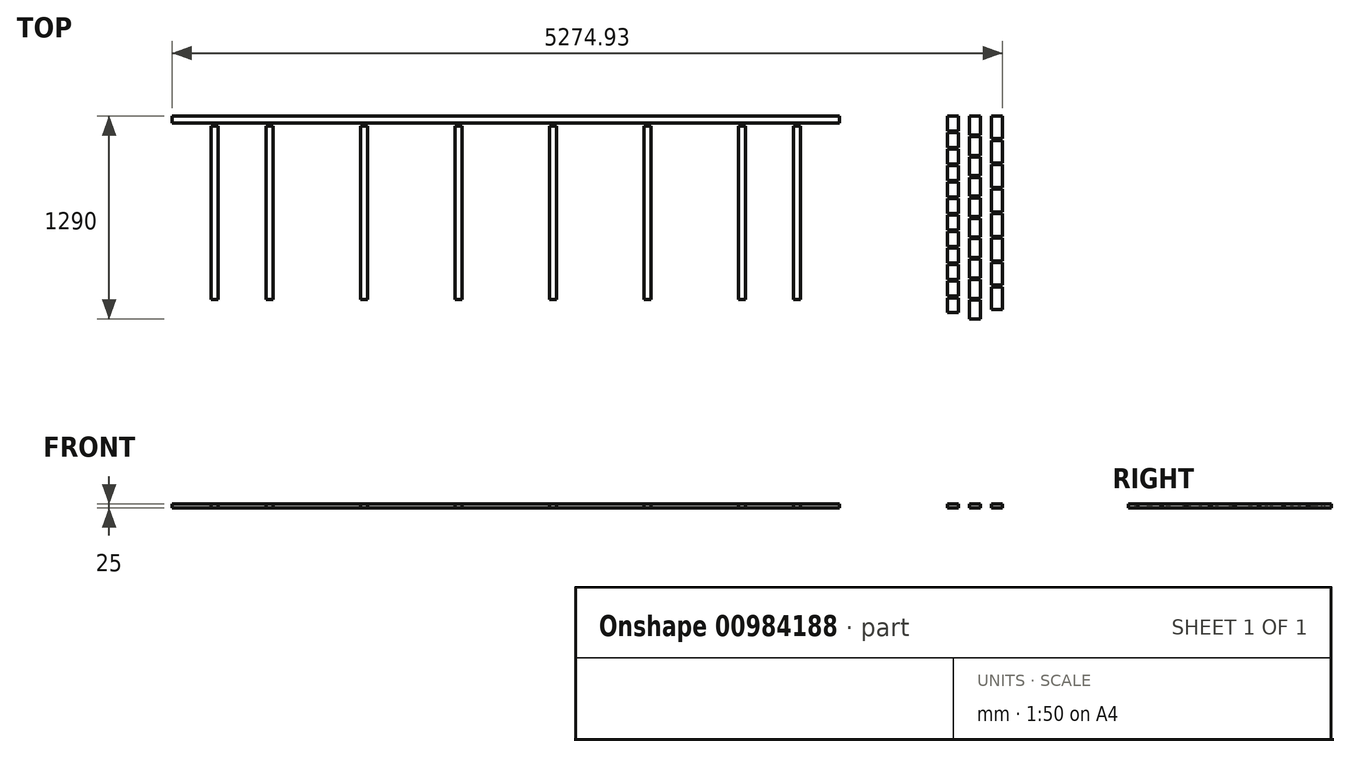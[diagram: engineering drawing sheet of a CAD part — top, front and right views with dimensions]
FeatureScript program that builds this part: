
annotation { "Feature Type Name" : "Feature", "Feature Type Description" : "" }
export const myFeature = defineFeature(function(context is Context, id is Id, definition is map)
    precondition{}
    {
        {
            var Q0;
            Q0=qCreatedBy(makeId("Top.planeOp"),FACE);
            var sketch = newSketch(context, id + "F0", { "sketchPlane" : qUnion([Q0])});
            skLineSegment(sketch, "E0.bottom", {"start": v(-2120, 45) * mm, "end": v(2120, 45) * mm});
            skLineSegment(sketch, "E0.top", {"start": v(-2120, 0) * mm, "end": v(2120, 0) * mm});
            skLineSegment(sketch, "E0.left", {"start": v(-2120, 45) * mm, "end": v(-2120, 0) * mm});
            skLineSegment(sketch, "E0.right", {"start": v(2120, 45) * mm, "end": v(2120, 0) * mm});
            skLineSegment(sketch, "E1.top", {"start": v(-1522.5, -1120) * mm, "end": v(-1477.5, -1120) * mm});
            skLineSegment(sketch, "E1.left", {"start": v(-1522.5, -20) * mm, "end": v(-1522.5, -1120) * mm});
            skLineSegment(sketch, "E1.right", {"start": v(-1477.5, -20) * mm, "end": v(-1477.5, -1120) * mm});
            skLineSegment(sketch, "E2.bottom", {"start": v(2804.93, 45) * mm, "end": v(2874.93, 45) * mm});
            skLineSegment(sketch, "E2.top", {"start": v(2804.93, -50) * mm, "end": v(2874.93, -50) * mm});
            skLineSegment(sketch, "E2.left", {"start": v(2804.93, 45) * mm, "end": v(2804.93, -50) * mm});
            skLineSegment(sketch, "E2.right", {"start": v(2874.93, 45) * mm, "end": v(2874.93, -50) * mm});
            skLineSegment(sketch, "E3.0.1.0", {"start": v(2804.93, -60) * mm, "end": v(2804.93, -155) * mm});
            skLineSegment(sketch, "E3.0.1.1", {"start": v(2804.93, -60) * mm, "end": v(2874.93, -60) * mm});
            skLineSegment(sketch, "E3.0.1.2", {"start": v(2804.93, -155) * mm, "end": v(2874.93, -155) * mm});
            skLineSegment(sketch, "E3.0.1.3", {"start": v(2874.93, -60) * mm, "end": v(2874.93, -155) * mm});
            skLineSegment(sketch, "E3.0.2.0", {"start": v(2804.93, -165) * mm, "end": v(2804.93, -260) * mm});
            skLineSegment(sketch, "E3.0.2.1", {"start": v(2804.93, -165) * mm, "end": v(2874.93, -165) * mm});
            skLineSegment(sketch, "E3.0.2.2", {"start": v(2804.93, -260) * mm, "end": v(2874.93, -260) * mm});
            skLineSegment(sketch, "E3.0.2.3", {"start": v(2874.93, -165) * mm, "end": v(2874.93, -260) * mm});
            skLineSegment(sketch, "E3.0.3.0", {"start": v(2804.93, -270) * mm, "end": v(2804.93, -365) * mm});
            skLineSegment(sketch, "E3.0.3.1", {"start": v(2804.93, -270) * mm, "end": v(2874.93, -270) * mm});
            skLineSegment(sketch, "E3.0.3.2", {"start": v(2804.93, -365) * mm, "end": v(2874.93, -365) * mm});
            skLineSegment(sketch, "E3.0.3.3", {"start": v(2874.93, -270) * mm, "end": v(2874.93, -365) * mm});
            skLineSegment(sketch, "E3.0.4.0", {"start": v(2804.93, -375) * mm, "end": v(2804.93, -470) * mm});
            skLineSegment(sketch, "E3.0.4.1", {"start": v(2804.93, -375) * mm, "end": v(2874.93, -375) * mm});
            skLineSegment(sketch, "E3.0.4.2", {"start": v(2804.93, -470) * mm, "end": v(2874.93, -470) * mm});
            skLineSegment(sketch, "E3.0.4.3", {"start": v(2874.93, -375) * mm, "end": v(2874.93, -470) * mm});
            skLineSegment(sketch, "E3.0.5.0", {"start": v(2804.93, -480) * mm, "end": v(2804.93, -575) * mm});
            skLineSegment(sketch, "E3.0.5.1", {"start": v(2804.93, -480) * mm, "end": v(2874.93, -480) * mm});
            skLineSegment(sketch, "E3.0.5.2", {"start": v(2804.93, -575) * mm, "end": v(2874.93, -575) * mm});
            skLineSegment(sketch, "E3.0.5.3", {"start": v(2874.93, -480) * mm, "end": v(2874.93, -575) * mm});
            skLineSegment(sketch, "E3.0.6.0", {"start": v(2804.93, -585) * mm, "end": v(2804.93, -680) * mm});
            skLineSegment(sketch, "E3.0.6.1", {"start": v(2804.93, -585) * mm, "end": v(2874.93, -585) * mm});
            skLineSegment(sketch, "E3.0.6.2", {"start": v(2804.93, -680) * mm, "end": v(2874.93, -680) * mm});
            skLineSegment(sketch, "E3.0.6.3", {"start": v(2874.93, -585) * mm, "end": v(2874.93, -680) * mm});
            skLineSegment(sketch, "E3.0.7.0", {"start": v(2804.93, -690) * mm, "end": v(2804.93, -785) * mm});
            skLineSegment(sketch, "E3.0.7.1", {"start": v(2804.93, -690) * mm, "end": v(2874.93, -690) * mm});
            skLineSegment(sketch, "E3.0.7.2", {"start": v(2804.93, -785) * mm, "end": v(2874.93, -785) * mm});
            skLineSegment(sketch, "E3.0.7.3", {"start": v(2874.93, -690) * mm, "end": v(2874.93, -785) * mm});
            skLineSegment(sketch, "E3.0.8.0", {"start": v(2804.93, -795) * mm, "end": v(2804.93, -890) * mm});
            skLineSegment(sketch, "E3.0.8.1", {"start": v(2804.93, -795) * mm, "end": v(2874.93, -795) * mm});
            skLineSegment(sketch, "E3.0.8.2", {"start": v(2804.93, -890) * mm, "end": v(2874.93, -890) * mm});
            skLineSegment(sketch, "E3.0.8.3", {"start": v(2874.93, -795) * mm, "end": v(2874.93, -890) * mm});
            skLineSegment(sketch, "E3.0.9.0", {"start": v(2804.93, -900) * mm, "end": v(2804.93, -995) * mm});
            skLineSegment(sketch, "E3.0.9.1", {"start": v(2804.93, -900) * mm, "end": v(2874.93, -900) * mm});
            skLineSegment(sketch, "E3.0.9.2", {"start": v(2804.93, -995) * mm, "end": v(2874.93, -995) * mm});
            skLineSegment(sketch, "E3.0.9.3", {"start": v(2874.93, -900) * mm, "end": v(2874.93, -995) * mm});
            skLineSegment(sketch, "E3.0.10.0", {"start": v(2804.93, -1005) * mm, "end": v(2804.93, -1100) * mm});
            skLineSegment(sketch, "E3.0.10.1", {"start": v(2804.93, -1005) * mm, "end": v(2874.93, -1005) * mm});
            skLineSegment(sketch, "E3.0.10.2", {"start": v(2804.93, -1100) * mm, "end": v(2874.93, -1100) * mm});
            skLineSegment(sketch, "E3.0.10.3", {"start": v(2874.93, -1005) * mm, "end": v(2874.93, -1100) * mm});
            skLineSegment(sketch, "E3.0.11.0", {"start": v(2804.93, -1110) * mm, "end": v(2804.93, -1205) * mm});
            skLineSegment(sketch, "E3.0.11.1", {"start": v(2804.93, -1110) * mm, "end": v(2874.93, -1110) * mm});
            skLineSegment(sketch, "E3.0.11.2", {"start": v(2804.93, -1205) * mm, "end": v(2874.93, -1205) * mm});
            skLineSegment(sketch, "E3.0.11.3", {"start": v(2874.93, -1110) * mm, "end": v(2874.93, -1205) * mm});
            skLineSegment(sketch, "E3.direction1", {"start": v(2531.99, -50) * mm, "end": v(2804.93, -50) * mm, "construction": true});
            skLineSegment(sketch, "E3.direction2", {"start": v(2804.93, -50) * mm, "end": v(2804.93, -155) * mm, "construction": true});
            skLineSegment(sketch, "E4.1.0.0", {"start": v(-922.5, -20) * mm, "end": v(-922.5, -1120) * mm});
            skLineSegment(sketch, "E4.1.0.1", {"start": v(-877.5, -20) * mm, "end": v(-877.5, -1120) * mm});
            skLineSegment(sketch, "E4.1.0.2", {"start": v(-922.5, -1120) * mm, "end": v(-877.5, -1120) * mm});
            skLineSegment(sketch, "E4.1.0.3", {"start": v(-922.5, -20) * mm, "end": v(-877.5, -20) * mm});
            skLineSegment(sketch, "E4.2.0.0", {"start": v(-322.5, -20) * mm, "end": v(-322.5, -1120) * mm});
            skLineSegment(sketch, "E4.2.0.1", {"start": v(-277.5, -20) * mm, "end": v(-277.5, -1120) * mm});
            skLineSegment(sketch, "E4.2.0.2", {"start": v(-322.5, -1120) * mm, "end": v(-277.5, -1120) * mm});
            skLineSegment(sketch, "E4.2.0.3", {"start": v(-322.5, -20) * mm, "end": v(-277.5, -20) * mm});
            skLineSegment(sketch, "E4.3.0.0", {"start": v(277.5, -20) * mm, "end": v(277.5, -1120) * mm});
            skLineSegment(sketch, "E4.3.0.1", {"start": v(322.5, -20) * mm, "end": v(322.5, -1120) * mm});
            skLineSegment(sketch, "E4.3.0.2", {"start": v(277.5, -1120) * mm, "end": v(322.5, -1120) * mm});
            skLineSegment(sketch, "E4.3.0.3", {"start": v(277.5, -20) * mm, "end": v(322.5, -20) * mm});
            skLineSegment(sketch, "E4.4.0.0", {"start": v(877.5, -20) * mm, "end": v(877.5, -1120) * mm});
            skLineSegment(sketch, "E4.4.0.1", {"start": v(922.5, -20) * mm, "end": v(922.5, -1120) * mm});
            skLineSegment(sketch, "E4.4.0.2", {"start": v(877.5, -1120) * mm, "end": v(922.5, -1120) * mm});
            skLineSegment(sketch, "E4.4.0.3", {"start": v(877.5, -20) * mm, "end": v(922.5, -20) * mm});
            skLineSegment(sketch, "E4.5.0.0", {"start": v(1477.5, -20) * mm, "end": v(1477.5, -1120) * mm});
            skLineSegment(sketch, "E4.5.0.1", {"start": v(1522.5, -20) * mm, "end": v(1522.5, -1120) * mm});
            skLineSegment(sketch, "E4.5.0.2", {"start": v(1477.5, -1120) * mm, "end": v(1522.5, -1120) * mm});
            skLineSegment(sketch, "E4.5.0.3", {"start": v(1477.5, -20) * mm, "end": v(1522.5, -20) * mm});
            skLineSegment(sketch, "E5.bottom", {"start": v(2944.93, 45) * mm, "end": v(3014.93, 45) * mm});
            skLineSegment(sketch, "E5.top", {"start": v(2944.93, -75) * mm, "end": v(3014.93, -75) * mm});
            skLineSegment(sketch, "E5.left", {"start": v(2944.93, 45) * mm, "end": v(2944.93, -75) * mm});
            skLineSegment(sketch, "E5.right", {"start": v(3014.93, 45) * mm, "end": v(3014.93, -75) * mm});
            skLineSegment(sketch, "E6.bottom", {"start": v(3084.93, 45) * mm, "end": v(3154.93, 45) * mm});
            skLineSegment(sketch, "E6.top", {"start": v(3084.93, -100) * mm, "end": v(3154.93, -100) * mm});
            skLineSegment(sketch, "E6.left", {"start": v(3084.93, 45) * mm, "end": v(3084.93, -100) * mm});
            skLineSegment(sketch, "E6.right", {"start": v(3154.93, 45) * mm, "end": v(3154.93, -100) * mm});
            skLineSegment(sketch, "E7", {"start": v(2874.93, 45) * mm, "end": v(2944.93, 45) * mm, "construction": true});
            skLineSegment(sketch, "E8", {"start": v(3014.93, 45) * mm, "end": v(3084.93, 45) * mm, "construction": true});
            skLineSegment(sketch, "E9.0.1.0", {"start": v(2944.93, -85) * mm, "end": v(3014.93, -85) * mm});
            skLineSegment(sketch, "E9.0.1.1", {"start": v(3014.93, -85) * mm, "end": v(3014.93, -205) * mm});
            skLineSegment(sketch, "E9.0.1.2", {"start": v(2944.93, -85) * mm, "end": v(2944.93, -205) * mm});
            skLineSegment(sketch, "E9.0.1.3", {"start": v(2944.93, -205) * mm, "end": v(3014.93, -205) * mm});
            skLineSegment(sketch, "E9.0.2.0", {"start": v(2944.93, -215) * mm, "end": v(3014.93, -215) * mm});
            skLineSegment(sketch, "E9.0.2.1", {"start": v(3014.93, -215) * mm, "end": v(3014.93, -335) * mm});
            skLineSegment(sketch, "E9.0.2.2", {"start": v(2944.93, -215) * mm, "end": v(2944.93, -335) * mm});
            skLineSegment(sketch, "E9.0.2.3", {"start": v(2944.93, -335) * mm, "end": v(3014.93, -335) * mm});
            skLineSegment(sketch, "E9.0.3.0", {"start": v(2944.93, -345) * mm, "end": v(3014.93, -345) * mm});
            skLineSegment(sketch, "E9.0.3.1", {"start": v(3014.93, -345) * mm, "end": v(3014.93, -465) * mm});
            skLineSegment(sketch, "E9.0.3.2", {"start": v(2944.93, -345) * mm, "end": v(2944.93, -465) * mm});
            skLineSegment(sketch, "E9.0.3.3", {"start": v(2944.93, -465) * mm, "end": v(3014.93, -465) * mm});
            skLineSegment(sketch, "E9.0.4.0", {"start": v(2944.93, -475) * mm, "end": v(3014.93, -475) * mm});
            skLineSegment(sketch, "E9.0.4.1", {"start": v(3014.93, -475) * mm, "end": v(3014.93, -595) * mm});
            skLineSegment(sketch, "E9.0.4.2", {"start": v(2944.93, -475) * mm, "end": v(2944.93, -595) * mm});
            skLineSegment(sketch, "E9.0.4.3", {"start": v(2944.93, -595) * mm, "end": v(3014.93, -595) * mm});
            skLineSegment(sketch, "E9.0.5.0", {"start": v(2944.93, -605) * mm, "end": v(3014.93, -605) * mm});
            skLineSegment(sketch, "E9.0.5.1", {"start": v(3014.93, -605) * mm, "end": v(3014.93, -725) * mm});
            skLineSegment(sketch, "E9.0.5.2", {"start": v(2944.93, -605) * mm, "end": v(2944.93, -725) * mm});
            skLineSegment(sketch, "E9.0.5.3", {"start": v(2944.93, -725) * mm, "end": v(3014.93, -725) * mm});
            skLineSegment(sketch, "E9.0.6.0", {"start": v(2944.93, -735) * mm, "end": v(3014.93, -735) * mm});
            skLineSegment(sketch, "E9.0.6.1", {"start": v(3014.93, -735) * mm, "end": v(3014.93, -855) * mm});
            skLineSegment(sketch, "E9.0.6.2", {"start": v(2944.93, -735) * mm, "end": v(2944.93, -855) * mm});
            skLineSegment(sketch, "E9.0.6.3", {"start": v(2944.93, -855) * mm, "end": v(3014.93, -855) * mm});
            skLineSegment(sketch, "E9.0.7.0", {"start": v(2944.93, -865) * mm, "end": v(3014.93, -865) * mm});
            skLineSegment(sketch, "E9.0.7.1", {"start": v(3014.93, -865) * mm, "end": v(3014.93, -985) * mm});
            skLineSegment(sketch, "E9.0.7.2", {"start": v(2944.93, -865) * mm, "end": v(2944.93, -985) * mm});
            skLineSegment(sketch, "E9.0.7.3", {"start": v(2944.93, -985) * mm, "end": v(3014.93, -985) * mm});
            skLineSegment(sketch, "E9.0.8.0", {"start": v(2944.93, -995) * mm, "end": v(3014.93, -995) * mm});
            skLineSegment(sketch, "E9.0.8.1", {"start": v(3014.93, -995) * mm, "end": v(3014.93, -1115) * mm});
            skLineSegment(sketch, "E9.0.8.2", {"start": v(2944.93, -995) * mm, "end": v(2944.93, -1115) * mm});
            skLineSegment(sketch, "E9.0.8.3", {"start": v(2944.93, -1115) * mm, "end": v(3014.93, -1115) * mm});
            skLineSegment(sketch, "E9.0.9.0", {"start": v(2944.93, -1125) * mm, "end": v(3014.93, -1125) * mm});
            skLineSegment(sketch, "E9.0.9.1", {"start": v(3014.93, -1125) * mm, "end": v(3014.93, -1245) * mm});
            skLineSegment(sketch, "E9.0.9.2", {"start": v(2944.93, -1125) * mm, "end": v(2944.93, -1245) * mm});
            skLineSegment(sketch, "E9.0.9.3", {"start": v(2944.93, -1245) * mm, "end": v(3014.93, -1245) * mm});
            skLineSegment(sketch, "E9.direction1", {"start": v(2366.4, -75) * mm, "end": v(2944.93, -75) * mm, "construction": true});
            skLineSegment(sketch, "E9.direction2", {"start": v(2944.93, -75) * mm, "end": v(2944.93, -205) * mm, "construction": true});
            skLineSegment(sketch, "E10.0.1.0", {"start": v(3084.93, -110) * mm, "end": v(3154.93, -110) * mm});
            skLineSegment(sketch, "E10.0.1.1", {"start": v(3084.93, -255) * mm, "end": v(3154.93, -255) * mm});
            skLineSegment(sketch, "E10.0.1.2", {"start": v(3154.93, -110) * mm, "end": v(3154.93, -255) * mm});
            skLineSegment(sketch, "E10.0.1.3", {"start": v(3084.93, -110) * mm, "end": v(3084.93, -255) * mm});
            skLineSegment(sketch, "E10.0.2.0", {"start": v(3084.93, -265) * mm, "end": v(3154.93, -265) * mm});
            skLineSegment(sketch, "E10.0.2.1", {"start": v(3084.93, -410) * mm, "end": v(3154.93, -410) * mm});
            skLineSegment(sketch, "E10.0.2.2", {"start": v(3154.93, -265) * mm, "end": v(3154.93, -410) * mm});
            skLineSegment(sketch, "E10.0.2.3", {"start": v(3084.93, -265) * mm, "end": v(3084.93, -410) * mm});
            skLineSegment(sketch, "E10.0.3.0", {"start": v(3084.93, -420) * mm, "end": v(3154.93, -420) * mm});
            skLineSegment(sketch, "E10.0.3.1", {"start": v(3084.93, -565) * mm, "end": v(3154.93, -565) * mm});
            skLineSegment(sketch, "E10.0.3.2", {"start": v(3154.93, -420) * mm, "end": v(3154.93, -565) * mm});
            skLineSegment(sketch, "E10.0.3.3", {"start": v(3084.93, -420) * mm, "end": v(3084.93, -565) * mm});
            skLineSegment(sketch, "E10.0.4.0", {"start": v(3084.93, -575) * mm, "end": v(3154.93, -575) * mm});
            skLineSegment(sketch, "E10.0.4.1", {"start": v(3084.93, -720) * mm, "end": v(3154.93, -720) * mm});
            skLineSegment(sketch, "E10.0.4.2", {"start": v(3154.93, -575) * mm, "end": v(3154.93, -720) * mm});
            skLineSegment(sketch, "E10.0.4.3", {"start": v(3084.93, -575) * mm, "end": v(3084.93, -720) * mm});
            skLineSegment(sketch, "E10.0.5.0", {"start": v(3084.93, -730) * mm, "end": v(3154.93, -730) * mm});
            skLineSegment(sketch, "E10.0.5.1", {"start": v(3084.93, -875) * mm, "end": v(3154.93, -875) * mm});
            skLineSegment(sketch, "E10.0.5.2", {"start": v(3154.93, -730) * mm, "end": v(3154.93, -875) * mm});
            skLineSegment(sketch, "E10.0.5.3", {"start": v(3084.93, -730) * mm, "end": v(3084.93, -875) * mm});
            skLineSegment(sketch, "E10.0.6.0", {"start": v(3084.93, -885) * mm, "end": v(3154.93, -885) * mm});
            skLineSegment(sketch, "E10.0.6.1", {"start": v(3084.93, -1030) * mm, "end": v(3154.93, -1030) * mm});
            skLineSegment(sketch, "E10.0.6.2", {"start": v(3154.93, -885) * mm, "end": v(3154.93, -1030) * mm});
            skLineSegment(sketch, "E10.0.6.3", {"start": v(3084.93, -885) * mm, "end": v(3084.93, -1030) * mm});
            skLineSegment(sketch, "E10.0.7.0", {"start": v(3084.93, -1040) * mm, "end": v(3154.93, -1040) * mm});
            skLineSegment(sketch, "E10.0.7.1", {"start": v(3084.93, -1185) * mm, "end": v(3154.93, -1185) * mm});
            skLineSegment(sketch, "E10.0.7.2", {"start": v(3154.93, -1040) * mm, "end": v(3154.93, -1185) * mm});
            skLineSegment(sketch, "E10.0.7.3", {"start": v(3084.93, -1040) * mm, "end": v(3084.93, -1185) * mm});
            skLineSegment(sketch, "E10.direction1", {"start": v(2556.76, -100) * mm, "end": v(3084.93, -100) * mm, "construction": true});
            skLineSegment(sketch, "E10.direction2", {"start": v(3084.93, -100) * mm, "end": v(3084.93, -255) * mm, "construction": true});
            skLineSegment(sketch, "E11.bottom", {"start": v(1827.5, -20) * mm, "end": v(1872.5, -20) * mm});
            skLineSegment(sketch, "E11.top", {"start": v(1827.5, -1120) * mm, "end": v(1872.5, -1120) * mm});
            skLineSegment(sketch, "E11.left", {"start": v(1827.5, -20) * mm, "end": v(1827.5, -1120) * mm});
            skLineSegment(sketch, "E11.right", {"start": v(1872.5, -20) * mm, "end": v(1872.5, -1120) * mm});
            skLineSegment(sketch, "E12.bottom", {"start": v(-1872.5, -20) * mm, "end": v(-1827.5, -20) * mm});
            skLineSegment(sketch, "E12.top", {"start": v(-1872.5, -1120) * mm, "end": v(-1827.5, -1120) * mm});
            skLineSegment(sketch, "E12.left", {"start": v(-1872.5, -20) * mm, "end": v(-1872.5, -1120) * mm});
            skLineSegment(sketch, "E12.right", {"start": v(-1827.5, -20) * mm, "end": v(-1827.5, -1120) * mm});
            skPoint(sketch, "E13", {"position": v(-2311.22, 234.17) * mm});
            skLineSegment(sketch, "E14", {"start": v(-1477.5, -1120) * mm, "end": v(1477.5, -1120) * mm, "construction": true});
            skPoint(sketch, "E15", {"position": v(0, 0) * mm});
            skLineSegment(sketch, "E16", {"start": v(-1522.5, -20) * mm, "end": v(-1477.5, -20) * mm});
            skLineSegment(sketch, "E17", {"start": v(0, 0) * mm, "end": v(0, -1120) * mm, "construction": true});
            skSolve(sketch);
        }
        {
            var Q0;
            Q0 = qSketchRegion(id + "F0", true);
            extrude(context, id + "F1", {"entities" : qUnion([Q0]), "depth" : 25 * mm, "offsetDistance" : 25 * mm});
        }
    });
